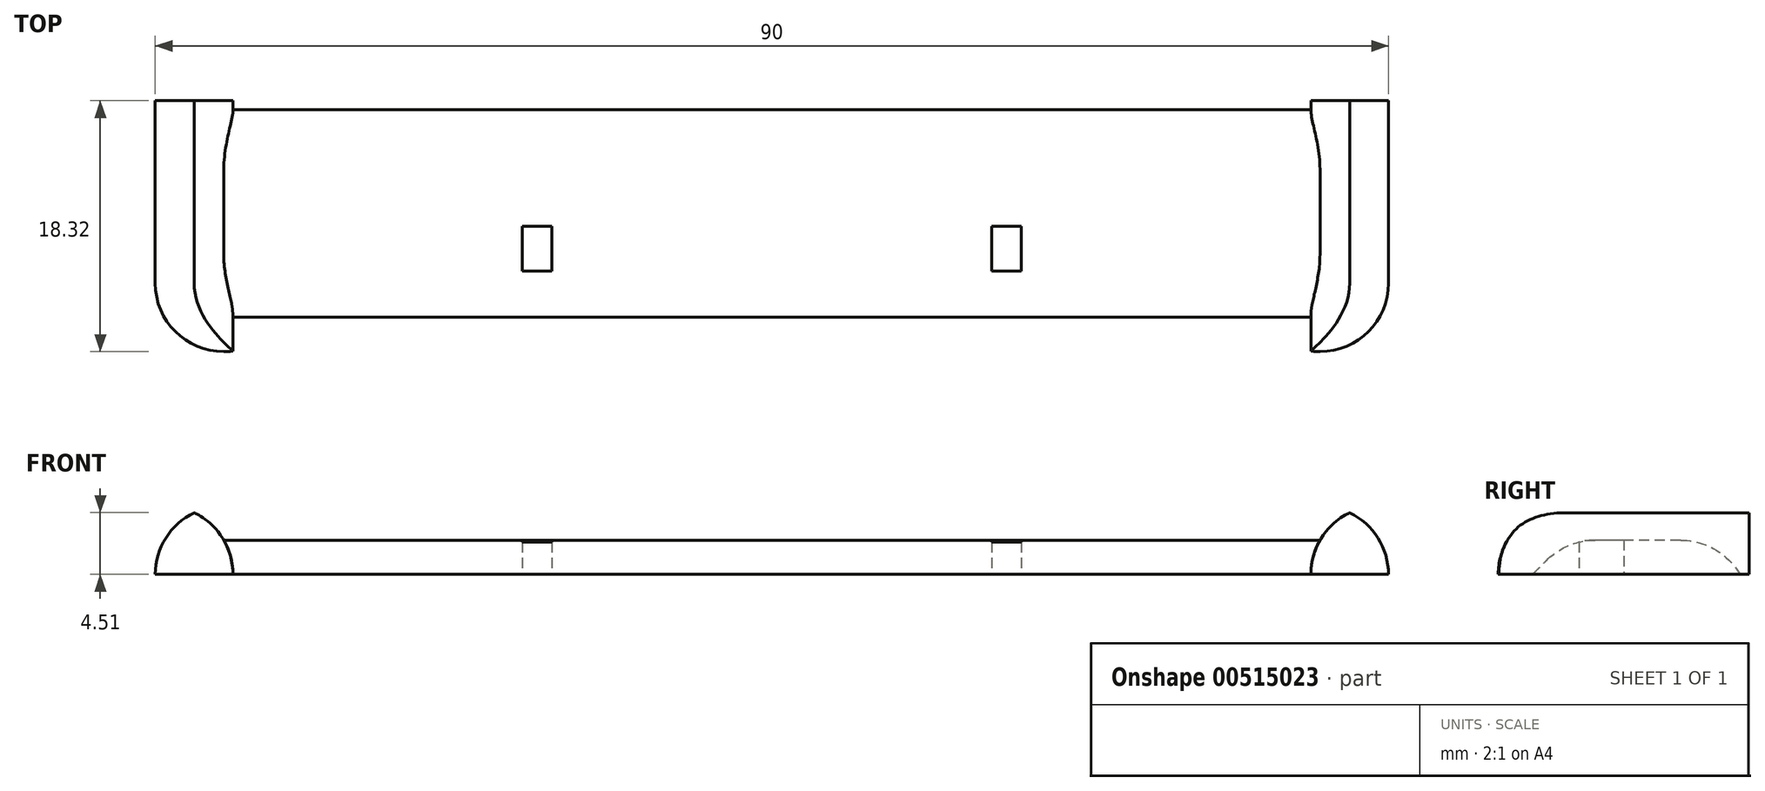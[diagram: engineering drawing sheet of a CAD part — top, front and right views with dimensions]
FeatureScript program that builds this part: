
annotation { "Feature Type Name" : "Feature", "Feature Type Description" : "" }
export const myFeature = defineFeature(function(context is Context, id is Id, definition is map)
    precondition{}
    {
        {
            var Q0;
            Q0=qCreatedBy(makeId("Top.planeOp"),FACE);
            var sketch = newSketch(context, id + "F0", { "sketchPlane" : qUnion([Q0])});
            skLineSegment(sketch, "E0.bottom", {"start": v(-16.46, 43.54) * mm, "end": v(73.54, 43.54) * mm});
            skLineSegment(sketch, "E0.top", {"start": v(-16.46, 25.22) * mm, "end": v(73.54, 25.22) * mm});
            skLineSegment(sketch, "E0.left", {"start": v(-16.46, 43.54) * mm, "end": v(-16.46, 25.22) * mm});
            skLineSegment(sketch, "E0.right", {"start": v(73.54, 43.54) * mm, "end": v(73.54, 25.22) * mm});
            skSolve(sketch);
        }
        {
            var Q0;
            Q0=makeQuery(id+"F0.imprint","IMPRINT",FACE,{"disambiguationData":[TD([[makeQuery(id+"F0.imprint","IMPRINT",EDGE,{"derivedFrom":sQuery(id+"F0.wireOp",EDGE,"E0.bottom")}),-1.0]])]});
            extrude(context, id + "F1", {"entities" : qUnion([Q0]), "depth" : 2.5 * mm, "offsetDistance" : 25 * mm});
        }
        {
            var Q0;
            Q0=makeQuery(id+"F1.opExtrude","CAP_FACE",FACE,{"disambiguationData":[OSD([sQuery(id+"F0.wireOp",EDGE,"E0.bottom"),sQuery(id+"F0.wireOp",EDGE,"E0.top"),sQuery(id+"F0.wireOp",EDGE,"E0.left"),sQuery(id+"F0.wireOp",EDGE,"E0.right")])],"isStart":true});
            var sketch = newSketch(context, id + "F2", { "sketchPlane" : qUnion([Q0])});
            skLineSegment(sketch, "E1", {"start": v(12.49, -34.38) * mm, "end": v(10.33, -34.38) * mm});
            skLineSegment(sketch, "E2", {"start": v(12.49, -34.38) * mm, "end": v(12.49, -31.11) * mm});
            skLineSegment(sketch, "E3", {"start": v(12.49, -31.11) * mm, "end": v(10.33, -31.11) * mm});
            skLineSegment(sketch, "E4", {"start": v(46.75, -34.38) * mm, "end": v(44.59, -34.38) * mm});
            skLineSegment(sketch, "E5", {"start": v(44.59, -34.38) * mm, "end": v(44.59, -31.11) * mm});
            skLineSegment(sketch, "E6", {"start": v(44.59, -31.11) * mm, "end": v(46.75, -31.11) * mm});
            skLineSegment(sketch, "E7", {"start": v(10.33, -31.11) * mm, "end": v(10.33, -34.38) * mm});
            skLineSegment(sketch, "E8", {"start": v(46.75, -31.11) * mm, "end": v(46.75, -34.38) * mm});
            skSolve(sketch);
        }
        {
            var Q0;
            {var subQ0=sQuery(id+"F2.wireOp",EDGE,"E1");Q0=makeQuery(id+"F2.imprint","IMPRINT",FACE,{"disambiguationData":[TD([[makeQuery(id+"F2.imprint","IMPRINT",EDGE,{"derivedFrom":subQ0}),-1.0]])]});}
            var Q1;
            Q1=makeQuery(id+"F2.imprint","IMPRINT",FACE,{"disambiguationData":[TD([[makeQuery(id+"F2.imprint","IMPRINT",EDGE,{"derivedFrom":sQuery(id+"F2.wireOp",EDGE,"E4")}),-1.0]])]});
            extrude(context, id + "F3", {"entities" : qUnion([Q0, Q1]), "operationType" : NewBodyOperationType.REMOVE, "oppositeDirection" : true, "depth" : 25 * mm, "offsetDistance" : 25 * mm});
        }
        {
            var Q0;
            Q0=makeQuery(id+"F1.opExtrude","CAP_FACE",FACE,{"disambiguationData":[OSD([sQuery(id+"F0.wireOp",EDGE,"E0.bottom"),sQuery(id+"F0.wireOp",EDGE,"E0.top"),sQuery(id+"F0.wireOp",EDGE,"E0.left"),sQuery(id+"F0.wireOp",EDGE,"E0.right")])],"isStart":false});
            var sketch = newSketch(context, id + "F4", { "sketchPlane" : qUnion([Q0])});
            skLineSegment(sketch, "E9", {"start": v(-16.46, 43.54) * mm, "end": v(-11.46, 43.54) * mm});
            skLineSegment(sketch, "E10", {"start": v(73.54, 43.54) * mm, "end": v(68.54, 43.54) * mm});
            skLineSegment(sketch, "E11", {"start": v(68.54, 43.54) * mm, "end": v(68.54, 25.22) * mm});
            skLineSegment(sketch, "E12", {"start": v(-11.46, 43.54) * mm, "end": v(-11.46, 25.22) * mm});
            skSolve(sketch);
        }
        {
            var Q0;
            Q0=makeQuery(id+"F4.imprint","IMPRINT",FACE,{"disambiguationData":[TD([[makeQuery(id+"F4.imprint","IMPRINT",EDGE,{"derivedFrom":sQuery(id+"F4.wireOp",EDGE,"E9")}),-1.0]])]});
            var Q1;
            Q1=makeQuery(id+"F4.imprint","IMPRINT",FACE,{"disambiguationData":[TD([[makeQuery(id+"F4.imprint","IMPRINT",EDGE,{"derivedFrom":sQuery(id+"F4.wireOp",EDGE,"E10")}),-1.0]])]});
            extrude(context, id + "F5", {"entities" : qUnion([Q0, Q1]), "operationType" : NewBodyOperationType.ADD, "depth" : 2.5 * mm, "offsetDistance" : 25 * mm});
        }
        {
            var Q0;
            Q0=makeQuery(id+"F5.opExtrude","CAP_EDGE",EDGE,{"disambiguationData":[OSD([sQuery(id+"F0.wireOp",EDGE,"E0.left")])],"isStart":false});
            var Q1;
            Q1=makeQuery(id+"F5.opExtrude","CAP_EDGE",EDGE,{"disambiguationData":[OSD([sQuery(id+"F4.wireOp",EDGE,"E12")])],"isStart":false});
            fillet(context, id + "F6", {"entities" : qUnion([Q0, Q1]), "radius" : 5 * mm, "tangentPropagation" : true, "allowEdgeOverflow" : false});
        }
        {
            var Q0;
            Q0=makeQuery(id+"F5.opExtrude","CAP_EDGE",EDGE,{"disambiguationData":[OSD([sQuery(id+"F4.wireOp",EDGE,"E11")])],"isStart":false});
            var Q1;
            Q1=makeQuery(id+"F5.opExtrude","CAP_EDGE",EDGE,{"disambiguationData":[OSD([sQuery(id+"F0.wireOp",EDGE,"E0.right")])],"isStart":false});
            fillet(context, id + "F7", {"entities" : qUnion([Q0, Q1]), "radius" : 5 * mm, "tangentPropagation" : true, "allowEdgeOverflow" : false});
        }
        {
            var Q0;
            Q0=makeQuery(id+"F1.opExtrude","CAP_EDGE",EDGE,{"disambiguationData":[OSD([sQuery(id+"F0.wireOp",EDGE,"E0.top")])],"isStart":false});
            chamfer(context, id + "F8", {"entities" : qUnion([Q0]), "width" : 5 * mm, "tangentPropagation" : true});
        }
        {
            var Q0;
            Q0=makeQuery(id+"F1.opExtrude","CAP_EDGE",EDGE,{"disambiguationData":[OSD([sQuery(id+"F0.wireOp",EDGE,"E0.bottom")])],"isStart":false});
            fillet(context, id + "F9", {"entities" : qUnion([Q0]), "radius" : 5 * mm, "tangentPropagation" : true, "allowEdgeOverflow" : false});
        }
        {
            var Q0;
            {var subQ0=sQuery(id+"F0.wireOp",EDGE,"E0.top");var subQ1=makeQuery(id+"F1.opExtrude","CAP_EDGE",EDGE,{"disambiguationData":[OSD([subQ0])],"isStart":false});var subQ2=sQuery(id+"F0.wireOp",EDGE,"E0.left");Q0=makeQuery(id+"F6.opFillet","BLEND_EDGE",EDGE,{"blendedFrom":[makeQuery(id+"F5.opExtrude","CAP_EDGE",EDGE,{"disambiguationData":[OSD([subQ2])],"isStart":false}),makeQuery(id+"F5.boolean.opBoolean","MERGE",FACE,{"derivedFrom":[makeQuery(id+"F1.opExtrude","SWEPT_FACE",FACE,{"disambiguationData":[OSD([subQ0])]}),makeQuery(id+"F5.opExtrude","SWEPT_FACE",FACE,{"disambiguationData":[OSD([subQ0]),TDD([makeQuery(id+"F4.imprint","IMPRINT",EDGE,{"disambiguationData":[TD([[makeQuery(id+"F4.imprint","INTERSECT",VERTEX,{"derivedFrom":[subQ1,makeQuery(id+"F1.opExtrude","CAP_EDGE",EDGE,{"disambiguationData":[OSD([subQ2])],"isStart":false})]}),-1.0]])],"derivedFrom":subQ1})])]}),makeQuery(id+"F5.opExtrude","SWEPT_FACE",FACE,{"disambiguationData":[OSD([subQ0]),TDD([makeQuery(id+"F4.imprint","IMPRINT",EDGE,{"disambiguationData":[TD([[makeQuery(id+"F4.imprint","INTERSECT",VERTEX,{"derivedFrom":[subQ1,makeQuery(id+"F1.opExtrude","CAP_EDGE",EDGE,{"disambiguationData":[OSD([sQuery(id+"F0.wireOp",EDGE,"E0.right")])],"isStart":false})]}),1.0]])],"derivedFrom":subQ1})])]})]})],"blendedInto":[makeQuery(id+"F5.boolean.opBoolean","MERGE",FACE,{"derivedFrom":[makeQuery(id+"F1.opExtrude","SWEPT_FACE",FACE,{"disambiguationData":[OSD([subQ0])]}),makeQuery(id+"F5.opExtrude","SWEPT_FACE",FACE,{"disambiguationData":[OSD([subQ0]),TDD([makeQuery(id+"F4.imprint","IMPRINT",EDGE,{"disambiguationData":[TD([[makeQuery(id+"F4.imprint","INTERSECT",VERTEX,{"derivedFrom":[subQ1,makeQuery(id+"F1.opExtrude","CAP_EDGE",EDGE,{"disambiguationData":[OSD([subQ2])],"isStart":false})]}),-1.0]])],"derivedFrom":subQ1})])]}),makeQuery(id+"F5.opExtrude","SWEPT_FACE",FACE,{"disambiguationData":[OSD([subQ0]),TDD([makeQuery(id+"F4.imprint","IMPRINT",EDGE,{"disambiguationData":[TD([[makeQuery(id+"F4.imprint","INTERSECT",VERTEX,{"derivedFrom":[subQ1,makeQuery(id+"F1.opExtrude","CAP_EDGE",EDGE,{"disambiguationData":[OSD([sQuery(id+"F0.wireOp",EDGE,"E0.right")])],"isStart":false})]}),1.0]])],"derivedFrom":subQ1})])]})]})]});}
            var Q1;
            {var subQ0=sQuery(id+"F0.wireOp",EDGE,"E0.right");var subQ1=sQuery(id+"F0.wireOp",EDGE,"E0.top");var subQ2=makeQuery(id+"F1.opExtrude","CAP_EDGE",EDGE,{"disambiguationData":[OSD([subQ1])],"isStart":false});Q1=makeQuery(id+"F7.opFillet","BLEND_EDGE",EDGE,{"blendedFrom":[makeQuery(id+"F5.opExtrude","CAP_EDGE",EDGE,{"disambiguationData":[OSD([subQ0])],"isStart":false}),makeQuery(id+"F5.boolean.opBoolean","MERGE",FACE,{"derivedFrom":[makeQuery(id+"F1.opExtrude","SWEPT_FACE",FACE,{"disambiguationData":[OSD([subQ1])]}),makeQuery(id+"F5.opExtrude","SWEPT_FACE",FACE,{"disambiguationData":[OSD([subQ1]),TDD([makeQuery(id+"F4.imprint","IMPRINT",EDGE,{"disambiguationData":[TD([[makeQuery(id+"F4.imprint","INTERSECT",VERTEX,{"derivedFrom":[subQ2,makeQuery(id+"F1.opExtrude","CAP_EDGE",EDGE,{"disambiguationData":[OSD([sQuery(id+"F0.wireOp",EDGE,"E0.left")])],"isStart":false})]}),-1.0]])],"derivedFrom":subQ2})])]}),makeQuery(id+"F5.opExtrude","SWEPT_FACE",FACE,{"disambiguationData":[OSD([subQ1]),TDD([makeQuery(id+"F4.imprint","IMPRINT",EDGE,{"disambiguationData":[TD([[makeQuery(id+"F4.imprint","INTERSECT",VERTEX,{"derivedFrom":[subQ2,makeQuery(id+"F1.opExtrude","CAP_EDGE",EDGE,{"disambiguationData":[OSD([subQ0])],"isStart":false})]}),1.0]])],"derivedFrom":subQ2})])]})]})],"blendedInto":[makeQuery(id+"F5.boolean.opBoolean","MERGE",FACE,{"derivedFrom":[makeQuery(id+"F1.opExtrude","SWEPT_FACE",FACE,{"disambiguationData":[OSD([subQ1])]}),makeQuery(id+"F5.opExtrude","SWEPT_FACE",FACE,{"disambiguationData":[OSD([subQ1]),TDD([makeQuery(id+"F4.imprint","IMPRINT",EDGE,{"disambiguationData":[TD([[makeQuery(id+"F4.imprint","INTERSECT",VERTEX,{"derivedFrom":[subQ2,makeQuery(id+"F1.opExtrude","CAP_EDGE",EDGE,{"disambiguationData":[OSD([sQuery(id+"F0.wireOp",EDGE,"E0.left")])],"isStart":false})]}),-1.0]])],"derivedFrom":subQ2})])]}),makeQuery(id+"F5.opExtrude","SWEPT_FACE",FACE,{"disambiguationData":[OSD([subQ1]),TDD([makeQuery(id+"F4.imprint","IMPRINT",EDGE,{"disambiguationData":[TD([[makeQuery(id+"F4.imprint","INTERSECT",VERTEX,{"derivedFrom":[subQ2,makeQuery(id+"F1.opExtrude","CAP_EDGE",EDGE,{"disambiguationData":[OSD([subQ0])],"isStart":false})]}),1.0]])],"derivedFrom":subQ2})])]})]})]});}
            fillet(context, id + "F10", {"entities" : qUnion([Q0, Q1]), "radius" : 5 * mm, "tangentPropagation" : true, "allowEdgeOverflow" : false});
        }
        {
            var Q0;
            {var subQ0=sQuery(id+"F0.wireOp",EDGE,"E0.top");Q0=makeQuery(id+"F8.opChamfer","BLEND_EDGE",EDGE,{"blendedFrom":[makeQuery(id+"F1.opExtrude","CAP_EDGE",EDGE,{"disambiguationData":[OSD([subQ0])],"isStart":false}),makeQuery(id+"F1.opExtrude","CAP_FACE",FACE,{"disambiguationData":[OSD([sQuery(id+"F0.wireOp",EDGE,"E0.bottom"),subQ0,sQuery(id+"F0.wireOp",EDGE,"E0.left"),sQuery(id+"F0.wireOp",EDGE,"E0.right")])],"isStart":false})],"blendedInto":[makeQuery(id+"F1.opExtrude","CAP_FACE",FACE,{"disambiguationData":[OSD([sQuery(id+"F0.wireOp",EDGE,"E0.bottom"),subQ0,sQuery(id+"F0.wireOp",EDGE,"E0.left"),sQuery(id+"F0.wireOp",EDGE,"E0.right")])],"isStart":false})]});}
            fillet(context, id + "F11", {"entities" : qUnion([Q0]), "radius" : 5 * mm, "tangentPropagation" : true, "allowEdgeOverflow" : false});
        }
    });
